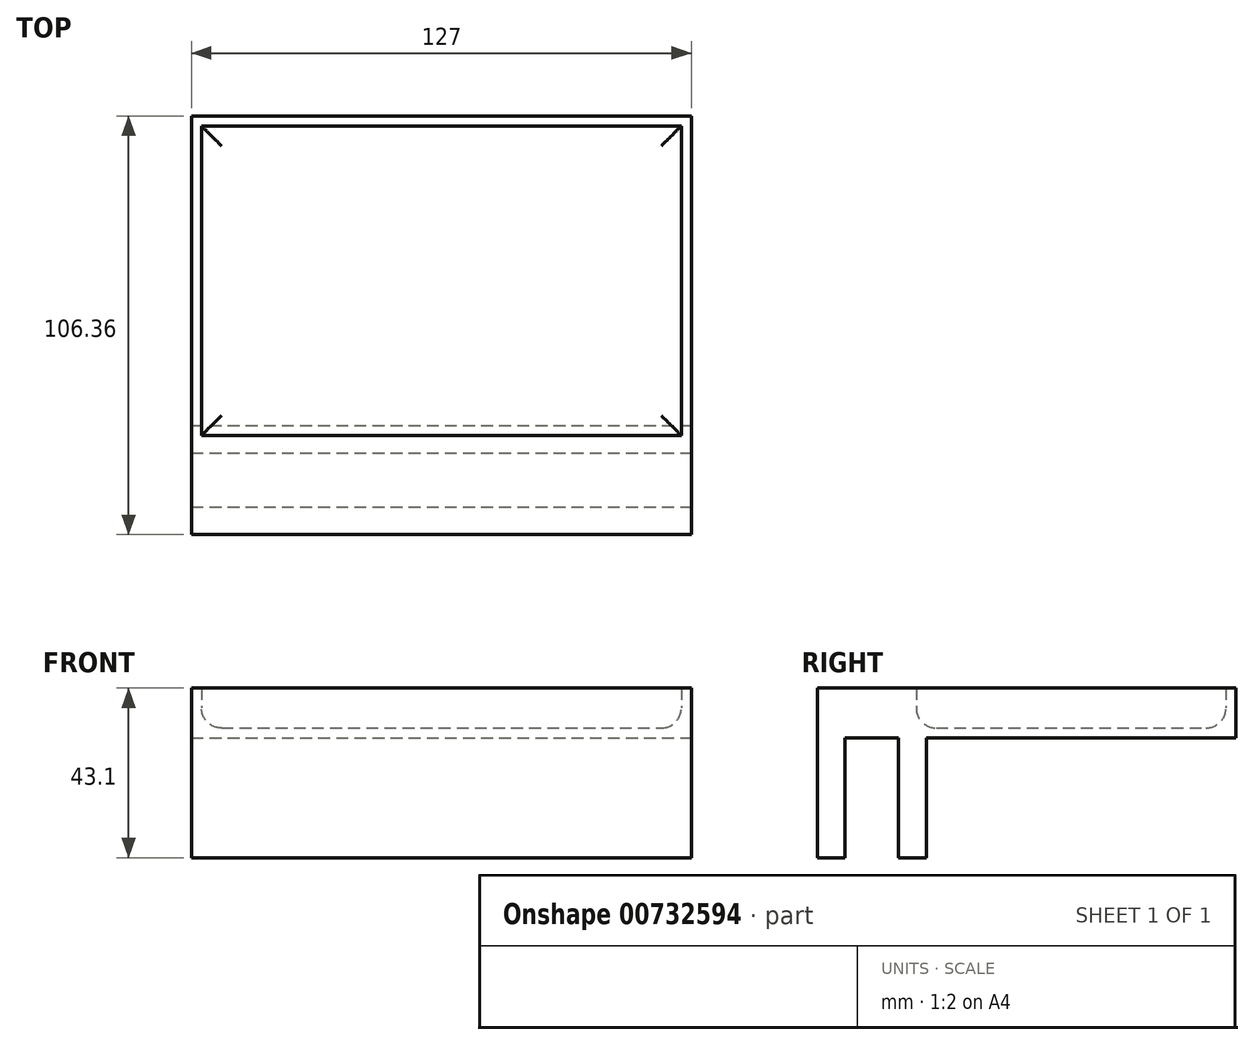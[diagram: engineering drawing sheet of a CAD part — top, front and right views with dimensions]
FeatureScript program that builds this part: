
annotation { "Feature Type Name" : "Feature", "Feature Type Description" : "" }
export const myFeature = defineFeature(function(context is Context, id is Id, definition is map)
    precondition{}
    {
        {
            var Q0;
            Q0=qCreatedBy(makeId("Right.planeOp"),FACE);
            var sketch = newSketch(context, id + "F0", { "sketchPlane" : qUnion([Q0])});
            skLineSegment(sketch, "E0", {"start": v(-57.55, -7.57) * mm, "end": v(-50.54, -7.57) * mm});
            skLineSegment(sketch, "E1", {"start": v(-50.54, -7.57) * mm, "end": v(-50.54, 22.83) * mm});
            skLineSegment(sketch, "E2", {"start": v(-50.54, 22.83) * mm, "end": v(-36.9, 22.83) * mm});
            skLineSegment(sketch, "E3", {"start": v(-36.9, 22.83) * mm, "end": v(-36.9, -7.57) * mm});
            skLineSegment(sketch, "E4", {"start": v(-36.9, -7.57) * mm, "end": v(-29.89, -7.57) * mm});
            skLineSegment(sketch, "E5", {"start": v(-29.89, -7.57) * mm, "end": v(-29.89, 22.83) * mm});
            skLineSegment(sketch, "E6", {"start": v(-29.89, 22.83) * mm, "end": v(-36.9, 22.83) * mm});
            skLineSegment(sketch, "E7", {"start": v(-50.54, 22.83) * mm, "end": v(-57.55, 22.83) * mm});
            skLineSegment(sketch, "E8", {"start": v(-57.55, 22.83) * mm, "end": v(-57.55, -7.57) * mm});
            skLineSegment(sketch, "E9", {"start": v(-57.55, 22.83) * mm, "end": v(-57.55, 31.38) * mm});
            skLineSegment(sketch, "E10", {"start": v(-29.89, 31.38) * mm, "end": v(-29.89, 22.83) * mm});
            skLineSegment(sketch, "E11.top", {"start": v(-29.89, 22.83) * mm, "end": v(48.81, 22.83) * mm});
            skLineSegment(sketch, "E11.right", {"start": v(48.81, 31.44) * mm, "end": v(48.81, 22.83) * mm});
            skLineSegment(sketch, "E12.top", {"start": v(-29.89, 35.53) * mm, "end": v(-25.52, 35.53) * mm});
            skLineSegment(sketch, "E12.left", {"start": v(-29.89, 31.38) * mm, "end": v(-29.89, 35.53) * mm});
            skLineSegment(sketch, "E13.top", {"start": v(47.23, 35.53) * mm, "end": v(48.81, 35.53) * mm});
            skLineSegment(sketch, "E13.right", {"start": v(48.81, 31.44) * mm, "end": v(48.81, 35.53) * mm});
            skLineSegment(sketch, "E14", {"start": v(-25.52, 35.53) * mm, "end": v(47.23, 35.53) * mm});
            skLineSegment(sketch, "E15", {"start": v(-29.89, 35.53) * mm, "end": v(-57.55, 35.53) * mm});
            skLineSegment(sketch, "E16", {"start": v(-57.55, 35.53) * mm, "end": v(-57.55, 31.38) * mm});
            skSolve(sketch);
        }
        {
            var Q0;
            Q0=makeQuery(id+"F0.imprint","IMPRINT",FACE,{"disambiguationData":[TD([[makeQuery(id+"F0.imprint","IMPRINT",EDGE,{"derivedFrom":sQuery(id+"F0.wireOp",EDGE,"E11.top")}),1.0]])]});
            var Q1;
            Q1=makeQuery(id+"F0.imprint","IMPRINT",FACE,{"disambiguationData":[TD([[makeQuery(id+"F0.imprint","IMPRINT",EDGE,{"derivedFrom":sQuery(id+"F0.wireOp",EDGE,"E13.bottom")}),1.0]])]});
            var Q2;
            Q2=makeQuery(id+"F0.imprint","IMPRINT",FACE,{"disambiguationData":[TD([[makeQuery(id+"F0.imprint","IMPRINT",EDGE,{"derivedFrom":sQuery(id+"F0.wireOp",EDGE,"E12.bottom")}),1.0]])]});
            var Q3;
            Q3=makeQuery(id+"F0.imprint","IMPRINT",FACE,{"disambiguationData":[TD([[makeQuery(id+"F0.imprint","IMPRINT",EDGE,{"derivedFrom":sQuery(id+"F0.wireOp",EDGE,"E0")}),1.0]])]});
            var Q4;
            Q4=makeQuery(id+"F0.imprint","IMPRINT",FACE,{"disambiguationData":[TD([[makeQuery(id+"F0.imprint","IMPRINT",EDGE,{"derivedFrom":sQuery(id+"F0.wireOp",EDGE,"E2")}),1.0]])]});
            var Q5;
            Q5=makeQuery(id+"F0.imprint","IMPRINT",FACE,{"disambiguationData":[TD([[makeQuery(id+"F0.imprint","IMPRINT",EDGE,{"derivedFrom":sQuery(id+"F0.wireOp",EDGE,"E3")}),1.0]])]});
            var Q6;
            {var subQ0=sQuery(id+"F0.wireOp",EDGE,"E12.right");Q6=makeQuery(id+"F0.imprint","IMPRINT",FACE,{"disambiguationData":[TD([[makeQuery(id+"F0.imprint","IMPRINT",EDGE,{"derivedFrom":subQ0}),-1.0]])]});}
            var Q7;
            Q7=makeQuery(id+"F0.imprint","IMPRINT",FACE,{"disambiguationData":[TD([[makeQuery(id+"F0.imprint","IMPRINT",EDGE,{"derivedFrom":sQuery(id+"F0.wireOp",EDGE,"wD3ydMSE-y03O-xQ5n-usI8-qgrb5It3hO6v.top")}),1.0]])]});
            var Q8;
            Q8=makeQuery(id+"F0.imprint","IMPRINT",FACE,{"disambiguationData":[TD([[makeQuery(id+"F0.imprint","IMPRINT",EDGE,{"derivedFrom":sQuery(id+"F0.wireOp",EDGE,"1MOa0dgL-UBlq-NqwH-2cKE-5gZrRT7ZLPll")}),1.0]])]});
            extrude(context, id + "F1", {"entities" : qUnion([Q0, Q1, Q2, Q3, Q4, Q5, Q6, Q7, Q8]), "endBound" : BoundingType.SYMMETRIC, "oppositeDirection" : true, "depth" : 127 * mm, "offsetDistance" : 25.4 * mm});
        }
        {
            var Q0;
            Q0=makeQuery(id+"F1.opExtrude","SWEPT_FACE",FACE,{"disambiguationData":[OSD([sQuery(id+"F0.wireOp",EDGE,"E12.top"),sQuery(id+"F0.wireOp",EDGE,"E13.top"),sQuery(id+"F0.wireOp",EDGE,"E14")])]});
            shell(context, id + "F2", {"entities" : qUnion([Q0]), "thickness" : 2.54 * mm});
        }
        {
            var Q0;
            Q0=makeQuery(id+"F2.opShell","OFFSET_FACE",FACE,{"disambiguationData":[OSD([sQuery(id+"F0.wireOp",EDGE,"E2")])]});
            extrude(context, id + "F3", {"entities" : qUnion([Q0]), "operationType" : NewBodyOperationType.ADD, "depth" : 10.16 * mm, "offsetDistance" : 25.4 * mm});
        }
        {
            var Q0;
            Q0=makeQuery(id+"F2.opShell","OFFSET_FACE",FACE,{"disambiguationData":[OSD([sQuery(id+"F0.wireOp",EDGE,"E0")])]});
            var Q1;
            Q1=makeQuery(id+"F2.opShell","OFFSET_FACE",FACE,{"disambiguationData":[OSD([sQuery(id+"F0.wireOp",EDGE,"E4")])]});
            var Q2;
            Q2=makeQuery(id+"F3.boolean.opBoolean","MERGE",FACE,{"derivedFrom":[makeQuery(id+"F1.opExtrude","SWEPT_FACE",FACE,{"disambiguationData":[OSD([sQuery(id+"F0.wireOp",EDGE,"E12.top"),sQuery(id+"F0.wireOp",EDGE,"E13.top"),sQuery(id+"F0.wireOp",EDGE,"E14"),sQuery(id+"F0.wireOp",EDGE,"E15")])]}),makeQuery(id+"F3.opExtrude","CAP_FACE",FACE,{"disambiguationData":[OSD([sQuery(id+"F0.wireOp",EDGE,"E2")])],"isStart":false})]});
            extrude(context, id + "F4", {"entities" : qUnion([Q0, Q1]), "operationType" : NewBodyOperationType.ADD, "depth" : 40.56 * mm, "offsetDistance" : 25.4 * mm});
        }
        {
            var Q0;
            Q0=makeQuery(id+"F2.opShell","OFFSET_FACE",FACE,{"disambiguationData":[OSD([sQuery(id+"F0.wireOp",EDGE,"E11.top")])]});
            fillet(context, id + "F5", {"entities" : qUnion([Q0]), "radius" : 5.08 * mm, "tangentPropagation" : true, "allowEdgeOverflow" : false});
        }
    });
